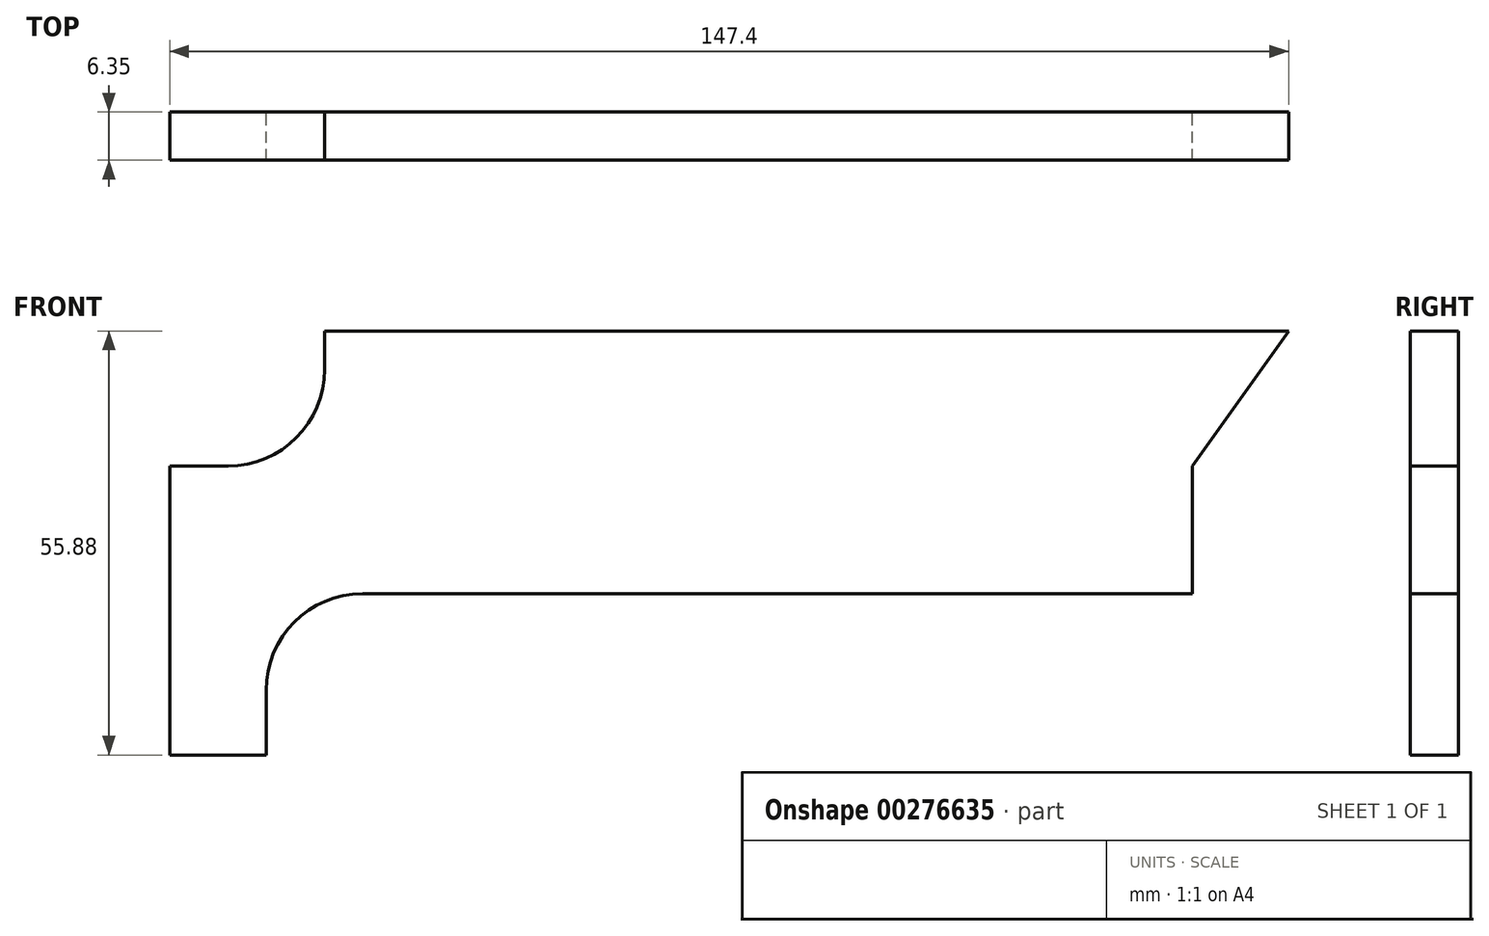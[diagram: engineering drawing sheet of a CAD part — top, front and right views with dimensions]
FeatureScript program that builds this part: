
annotation { "Feature Type Name" : "Feature", "Feature Type Description" : "" }
export const myFeature = defineFeature(function(context is Context, id is Id, definition is map)
    precondition{}
    {
        {
            var Q0;
            Q0=qCreatedBy(makeId("Front.planeOp"),FACE);
            var sketch = newSketch(context, id + "F0", { "sketchPlane" : qUnion([Q0])});
            skPoint(sketch, "E0", {"position": v(12.7, 0) * mm});
            skLineSegment(sketch, "E1", {"start": v(0, 0) * mm, "end": v(12.7, 0) * mm});
            skPoint(sketch, "E2", {"position": v(147.4, 55.88) * mm});
            skPoint(sketch, "E3", {"position": v(0, 38.1) * mm});
            skLineSegment(sketch, "E4", {"start": v(0, 0) * mm, "end": v(0, 38.1) * mm});
            skPoint(sketch, "E5", {"position": v(20.4, 38.1) * mm});
            skPoint(sketch, "E6", {"position": v(20.4, 55.88) * mm});
            skLineSegment(sketch, "E7", {"start": v(0, 38.1) * mm, "end": v(7.7, 38.1) * mm});
            skLineSegment(sketch, "E8", {"start": v(20.4, 50.8) * mm, "end": v(20.4, 55.88) * mm});
            skLineSegment(sketch, "E9", {"start": v(20.4, 55.88) * mm, "end": v(147.4, 55.88) * mm});
            skArc(sketch, "E10.filletArc", {"start": v(7.7, 38.1) * mm, "mid": v(16.68, 41.82) * mm, "end": v(20.4, 50.8) * mm});
            skPoint(sketch, "E11", {"position": v(12.7, 21.24) * mm});
            skLineSegment(sketch, "E12", {"start": v(12.7, 0) * mm, "end": v(12.7, 8.54) * mm});
            skArc(sketch, "E13.filletArc", {"start": v(25.4, 21.24) * mm, "mid": v(16.42, 17.52) * mm, "end": v(12.7, 8.54) * mm});
            skPoint(sketch, "E14", {"position": v(134.7, 38.1) * mm});
            skPoint(sketch, "E15", {"position": v(134.7, 21.24) * mm});
            skLineSegment(sketch, "E16", {"start": v(134.7, 21.24) * mm, "end": v(134.7, 38.1) * mm});
            skLineSegment(sketch, "E17", {"start": v(25.4, 21.24) * mm, "end": v(134.7, 21.24) * mm});
            skLineSegment(sketch, "E18", {"start": v(134.7, 38.1) * mm, "end": v(147.4, 55.88) * mm});
            skSolve(sketch);
        }
        {
            var Q0;
            Q0 = qSketchRegion(id + "F0", true);
            extrude(context, id + "F1", {"entities" : qUnion([Q0]), "depth" : 6.35 * mm});
        }
    });
